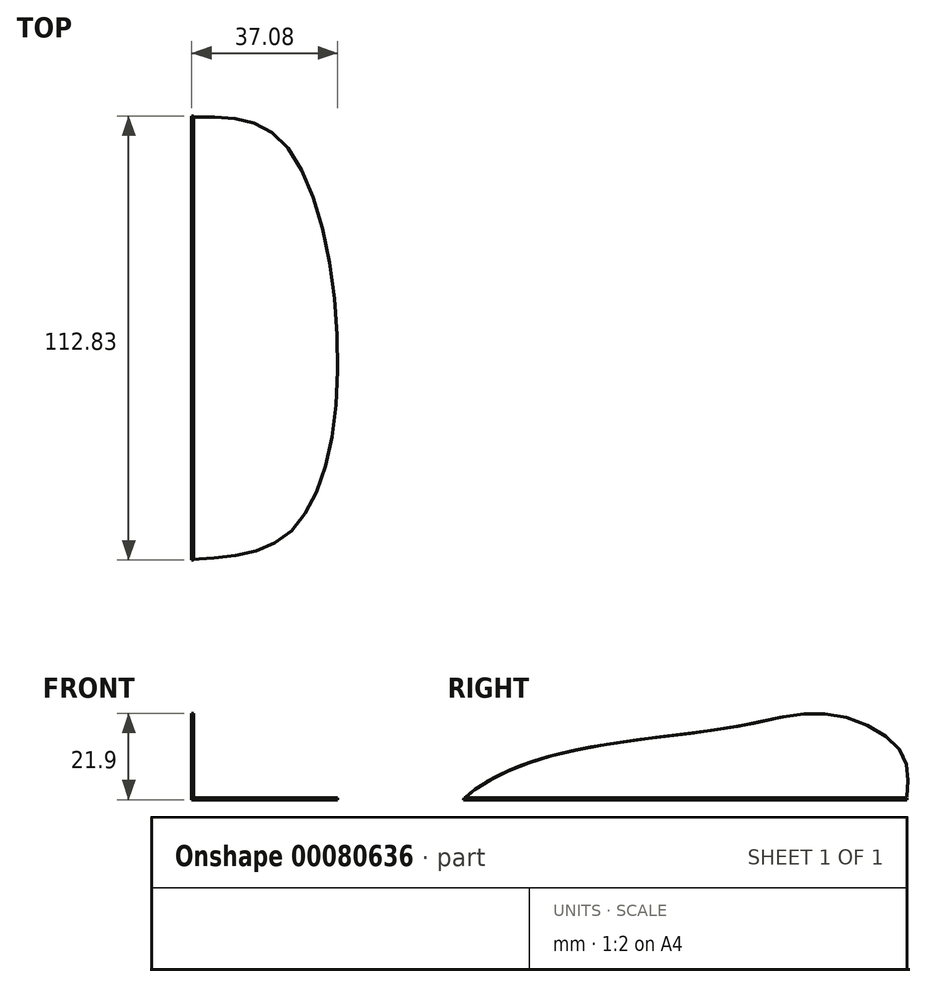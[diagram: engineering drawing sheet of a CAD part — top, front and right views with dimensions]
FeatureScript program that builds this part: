
annotation { "Feature Type Name" : "Feature", "Feature Type Description" : "" }
export const myFeature = defineFeature(function(context is Context, id is Id, definition is map)
    precondition{}
    {
        {
            var Q0;
            Q0=qCreatedBy(makeId("Top.planeOp"),FACE);
            var sketch = newSketch(context, id + "F0", { "sketchPlane" : qUnion([Q0])});
            skLineSegment(sketch, "E0", {"start": v(0, 56.27) * mm, "end": v(0, -56.12) * mm});
            skFitSpline(sketch, "E1", {"points": [v(0, 56.27) * mm, v(22.53, 50.57) * mm, v(37.08, -6.48) * mm, v(24.53, -49.56) * mm, v(0, -56.12) * mm], "startDerivative": vector(123.22, 2.7) * mm, "endDerivative": vector(-130.6, -6.95) * mm});
            skSolve(sketch);
        }
        {
            var Q0;
            Q0=qCreatedBy(makeId("Right.planeOp"),FACE);
            var sketch = newSketch(context, id + "F1", { "sketchPlane" : qUnion([Q0])});
            skFitSpline(sketch, "E2", {"points": [v(-56.25, 0) * mm, v(-46.29, 6.68) * mm, v(-20.7, 13.92) * mm, v(14.84, 18.9) * mm, v(37.25, 21.62) * mm, v(54.91, 12.11) * mm, v(56.27, 0) * mm], "startDerivative": vector(27.72, 40.02) * mm, "endDerivative": vector(-6.95, -102.44) * mm});
            skLineSegment(sketch, "E3", {"start": v(-56.25, 0) * mm, "end": v(56.27, 0) * mm});
            skSolve(sketch);
        }
        {
            var Q0;
            Q0=makeQuery(id+"F0.imprint","IMPRINT",FACE,{"disambiguationData":[TD([[makeQuery(id+"F0.imprint","IMPRINT",EDGE,{"derivedFrom":sQuery(id+"F0.wireOp",EDGE,"E0")}),1.0]])]});
            extrude(context, id + "F2", {"entities" : qUnion([Q0]), "depth" : .5 * mm});
        }
        {
            var Q0;
            Q0=makeQuery(id+"F1.imprint","IMPRINT",FACE,{"disambiguationData":[TD([[makeQuery(id+"F1.imprint","IMPRINT",EDGE,{"derivedFrom":sQuery(id+"F1.wireOp",EDGE,"E2")}),-1.0]])]});
            extrude(context, id + "F3", {"entities" : qUnion([Q0]), "operationType" : NewBodyOperationType.ADD, "depth" : .5 * mm});
        }
    });
